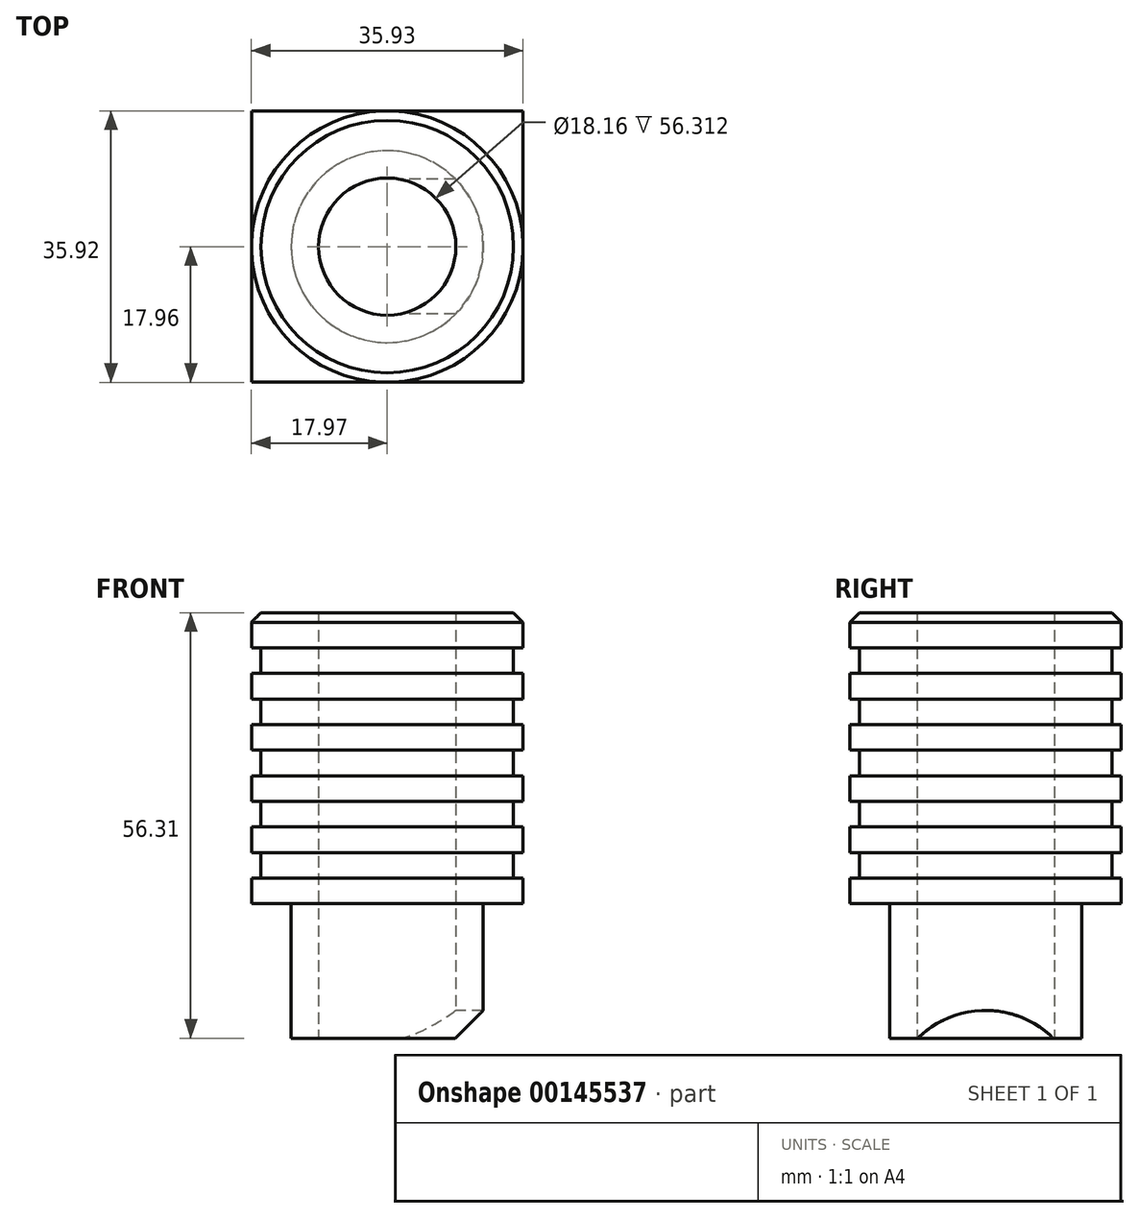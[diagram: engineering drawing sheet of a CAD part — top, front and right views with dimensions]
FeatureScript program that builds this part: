
annotation { "Feature Type Name" : "Feature", "Feature Type Description" : "" }
export const myFeature = defineFeature(function(context is Context, id is Id, definition is map)
    precondition{}
    {
        {
            var Q0;
            Q0=qCreatedBy(makeId("Front.planeOp"),FACE);
            var sketch = newSketch(context, id + "F0", { "sketchPlane" : qUnion([Q0])});
            skLineSegment(sketch, "E0", {"start": v(0, 0) * mm, "end": v(0, 55.04) * mm});
            skLineSegment(sketch, "E1", {"start": v(12.9, 55.04) * mm, "end": v(50.8, 55.04) * mm});
            skLineSegment(sketch, "E2", {"start": v(50.8, 55.04) * mm, "end": v(50.8, 51.66) * mm});
            skLineSegment(sketch, "E3", {"start": v(0, 55.04) * mm, "end": v(0, 56.31) * mm});
            skLineSegment(sketch, "E4", {"start": v(12.9, 56.31) * mm, "end": v(16.7, 56.31) * mm});
            skLineSegment(sketch, "E5", {"start": v(16.7, 56.31) * mm, "end": v(17.97, 55.04) * mm});
            skLineSegment(sketch, "E6", {"start": v(17.97, 55.04) * mm, "end": v(12.9, 55.04) * mm});
            skLineSegment(sketch, "E7", {"start": v(16.7, 51.66) * mm, "end": v(50.8, 51.66) * mm});
            skLineSegment(sketch, "E8", {"start": v(16.7, 48.27) * mm, "end": v(50.8, 48.27) * mm});
            skLineSegment(sketch, "E9", {"start": v(16.7, 44.88) * mm, "end": v(50.8, 44.88) * mm});
            skLineSegment(sketch, "E10.bottom", {"start": v(16.7, 41.5) * mm, "end": v(50.8, 41.5) * mm});
            skLineSegment(sketch, "E10.top", {"start": v(16.7, 38.1) * mm, "end": v(50.8, 38.1) * mm});
            skLineSegment(sketch, "E10.right", {"start": v(50.8, 41.5) * mm, "end": v(50.8, 38.1) * mm});
            skLineSegment(sketch, "E11.bottom", {"start": v(16.7, 34.72) * mm, "end": v(50.8, 34.72) * mm});
            skLineSegment(sketch, "E11.top", {"start": v(16.7, 31.34) * mm, "end": v(50.8, 31.34) * mm});
            skLineSegment(sketch, "E11.right", {"start": v(50.8, 34.72) * mm, "end": v(50.8, 31.34) * mm});
            skLineSegment(sketch, "E12.bottom", {"start": v(16.7, 27.95) * mm, "end": v(50.8, 27.95) * mm});
            skLineSegment(sketch, "E12.top", {"start": v(16.7, 24.56) * mm, "end": v(50.8, 24.56) * mm});
            skLineSegment(sketch, "E12.right", {"start": v(50.8, 27.95) * mm, "end": v(50.8, 24.56) * mm});
            skLineSegment(sketch, "E13.bottom", {"start": v(16.7, 21.18) * mm, "end": v(50.8, 21.18) * mm});
            skLineSegment(sketch, "E13.top", {"start": v(17.97, 17.79) * mm, "end": v(50.8, 17.79) * mm});
            skLineSegment(sketch, "E13.right", {"start": v(50.8, 21.18) * mm, "end": v(50.8, 17.79) * mm});
            skLineSegment(sketch, "E14.trimOffspring", {"start": v(50.8, 48.27) * mm, "end": v(50.8, 44.88) * mm});
            skLineSegment(sketch, "E15", {"start": v(12.9, 17.79) * mm, "end": v(12.9, 56.31) * mm});
            skLineSegment(sketch, "E16", {"start": v(16.7, 51.66) * mm, "end": v(16.7, 48.27) * mm});
            skLineSegment(sketch, "E17", {"start": v(16.7, 44.88) * mm, "end": v(16.7, 41.5) * mm});
            skLineSegment(sketch, "E18", {"start": v(16.7, 38.1) * mm, "end": v(16.7, 34.72) * mm});
            skLineSegment(sketch, "E19", {"start": v(16.7, 31.34) * mm, "end": v(16.7, 27.95) * mm});
            skLineSegment(sketch, "E20", {"start": v(16.7, 24.56) * mm, "end": v(16.7, 21.18) * mm});
            skLineSegment(sketch, "E21", {"start": v(9.08, 0) * mm, "end": v(12.7, 0) * mm});
            skLineSegment(sketch, "E22", {"start": v(17.97, 17.79) * mm, "end": v(12.9, 17.79) * mm});
            skLineSegment(sketch, "E23", {"start": v(12.7, 0) * mm, "end": v(12.7, 17.79) * mm});
            skLineSegment(sketch, "E24", {"start": v(12.9, 17.79) * mm, "end": v(12.7, 17.79) * mm});
            skLineSegment(sketch, "E25", {"start": v(9.08, 0) * mm, "end": v(9.08, 56.31) * mm});
            skLineSegment(sketch, "E26", {"start": v(9.08, 56.31) * mm, "end": v(12.9, 56.31) * mm});
            skSolve(sketch);
        }
        {
            var Q0;
            Q0 = qSketchRegion(id + "F0", true);
            var Q1;
            Q1=sQuery(id+"F0.wireOp",EDGE,"E0");
            revolve(context, id + "F1", {"entities" : qUnion([Q0]), "axis" : qUnion([Q1]), "revolveType" : RevolveType.FULL});
        }
        {
            var Q0;
            Q0=makeQuery(id+"F1.opRevolve","SWEPT_FACE",FACE,{"disambiguationData":[OSD([sQuery(id+"F0.wireOp",EDGE,"E4")])]});
            var sketch = newSketch(context, id + "F2", { "sketchPlane" : qUnion([Q0])});
            skLineSegment(sketch, "E27.bottom", {"start": v(-17.96, 17.96) * mm, "end": v(17.96, 17.96) * mm});
            skLineSegment(sketch, "E27.top", {"start": v(-17.96, -17.96) * mm, "end": v(17.96, -17.96) * mm});
            skLineSegment(sketch, "E27.left", {"start": v(-17.96, 17.96) * mm, "end": v(-17.96, -17.96) * mm});
            skLineSegment(sketch, "E27.right", {"start": v(17.96, 17.96) * mm, "end": v(17.96, -17.96) * mm});
            skLineSegment(sketch, "E28.bottom", {"start": v(-50.8, 50.8) * mm, "end": v(50.8, 50.8) * mm});
            skLineSegment(sketch, "E28.top", {"start": v(-50.8, -50.8) * mm, "end": v(50.8, -50.8) * mm});
            skLineSegment(sketch, "E28.left", {"start": v(-50.8, 50.8) * mm, "end": v(-50.8, -50.8) * mm});
            skLineSegment(sketch, "E28.right", {"start": v(50.8, 50.8) * mm, "end": v(50.8, -50.8) * mm});
            skCircle(sketch, "E29.0", {"center": v(0, 0) * mm, "radius": 50.8 * mm});
            skSolve(sketch);
        }
        {
            var Q0;
            Q0=makeQuery(id+"F2.imprint","IMPRINT",FACE,{"disambiguationData":[TD([[makeQuery(id+"F2.imprint","IMPRINT",EDGE,{"derivedFrom":sQuery(id+"F2.wireOp",EDGE,"E27.bottom")}),1.0]])]});
            extrude(context, id + "F3", {"entities" : qUnion([Q0]), "operationType" : NewBodyOperationType.REMOVE, "endBound" : BoundingType.THROUGH_ALL, "oppositeDirection" : true, "depth" : 25.4 * mm});
        }
        {
            var Q0;
            Q0=qCreatedBy(makeId("Right.planeOp"),FACE);
            var sketch = newSketch(context, id + "F4", { "sketchPlane" : qUnion([Q0])});
            skCircle(sketch, "E30", {"center": v(0, -9.01) * mm, "radius": 12.7 * mm});
            skLineSegment(sketch, "E31", {"start": v(-8.94, 0) * mm, "end": v(8.94, 0) * mm});
            skPoint(sketch, "E32", {"position": v(0, 3.68) * mm});
            skPoint(sketch, "E33", {"position": v(0, 0) * mm});
            skSolve(sketch);
        }
        {
            var Q0;
            Q0 = qSketchRegion(id + "F4", true);
            var Q1;
            Q1=makeQuery(id+"F1.opRevolve","SWEPT_FACE",FACE,{"disambiguationData":[OSD([sQuery(id+"F0.wireOp",EDGE,"E23")])]});
            extrude(context, id + "F5", {"entities" : qUnion([Q0]), "operationType" : NewBodyOperationType.REMOVE, "endBound" : BoundingType.UP_TO_SURFACE, "endBoundEntityFace" : qUnion([Q1]), "depth" : 25.4 * mm});
        }
    });
